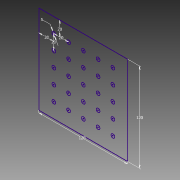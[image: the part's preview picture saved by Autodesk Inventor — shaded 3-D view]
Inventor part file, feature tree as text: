
AUTODESK INVENTOR PART (.ipt)
format: ipt  version: 2015 (Build 190159000, 159)  size: 75,264 bytes
history: native  units: mm
features: sketch x1
ambient origin geometry x8: Origin, YZ Plane, XZ Plane, XY Plane, X Axis, Y Axis, Z Axis, Center Point
feature tree (1):
  sketch  "Sketch1"  dims[d0=120.0mm d1=120.0mm d2=5.0mm d4=20.0mm d5=20.0mm d6=50.0mm d8=20.0mm d9=50.0mm d11=20.0mm]
